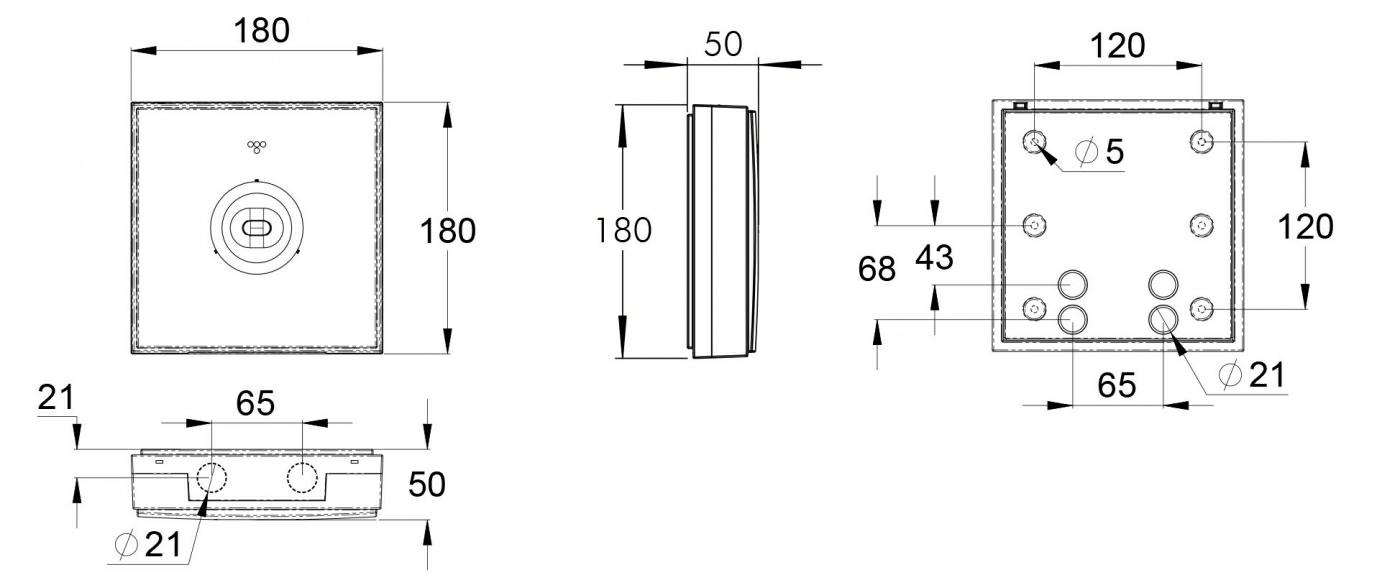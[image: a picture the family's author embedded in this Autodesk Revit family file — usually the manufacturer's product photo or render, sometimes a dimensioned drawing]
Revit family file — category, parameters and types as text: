
# Revit family: ROBUST EXIT LED EMERGENCY EXIT LIGHT TWT9651W
name_source: partatom
category: Lighting Fixtures
revit_build: Autodesk Revit 2015 (Build: 20160512_0715(x64)
units: mm (PartAtom-declared; Revit-internal decimal feet)

## types (3) — shared parameters
Body Material = Plastic
Depth = 126 mm  [stored 0.413386 ft]
Height = 126 mm  [stored 0.413386 ft]
Keynote = 23
Manufacturer = Teknoware Oy
Model = ROBUST EXIT
Product Code = TWT9651W
Type Image = <None>
Width = 304 mm  [stored 0.997375 ft]

## per-type parameters (varying)
| type | Down | Left | Pictogram | Right |
| -arrow down | Yes | No | Teknoware Pictogram PB9604E | No |
| -arrow left | No | Yes | Teknoware Pictogram PB9605E | No |
| -arrow right | No | No | Teknoware Pictogram PB9606E | Yes |

note: [stored X ft] marks values corroborated as IEEE doubles in the binary element streams (Revit-internal decimal feet)

## geometry (parser evidence)
native form markers: Blend x6, Sweep x13
no freeform markers — native parametric forms only
